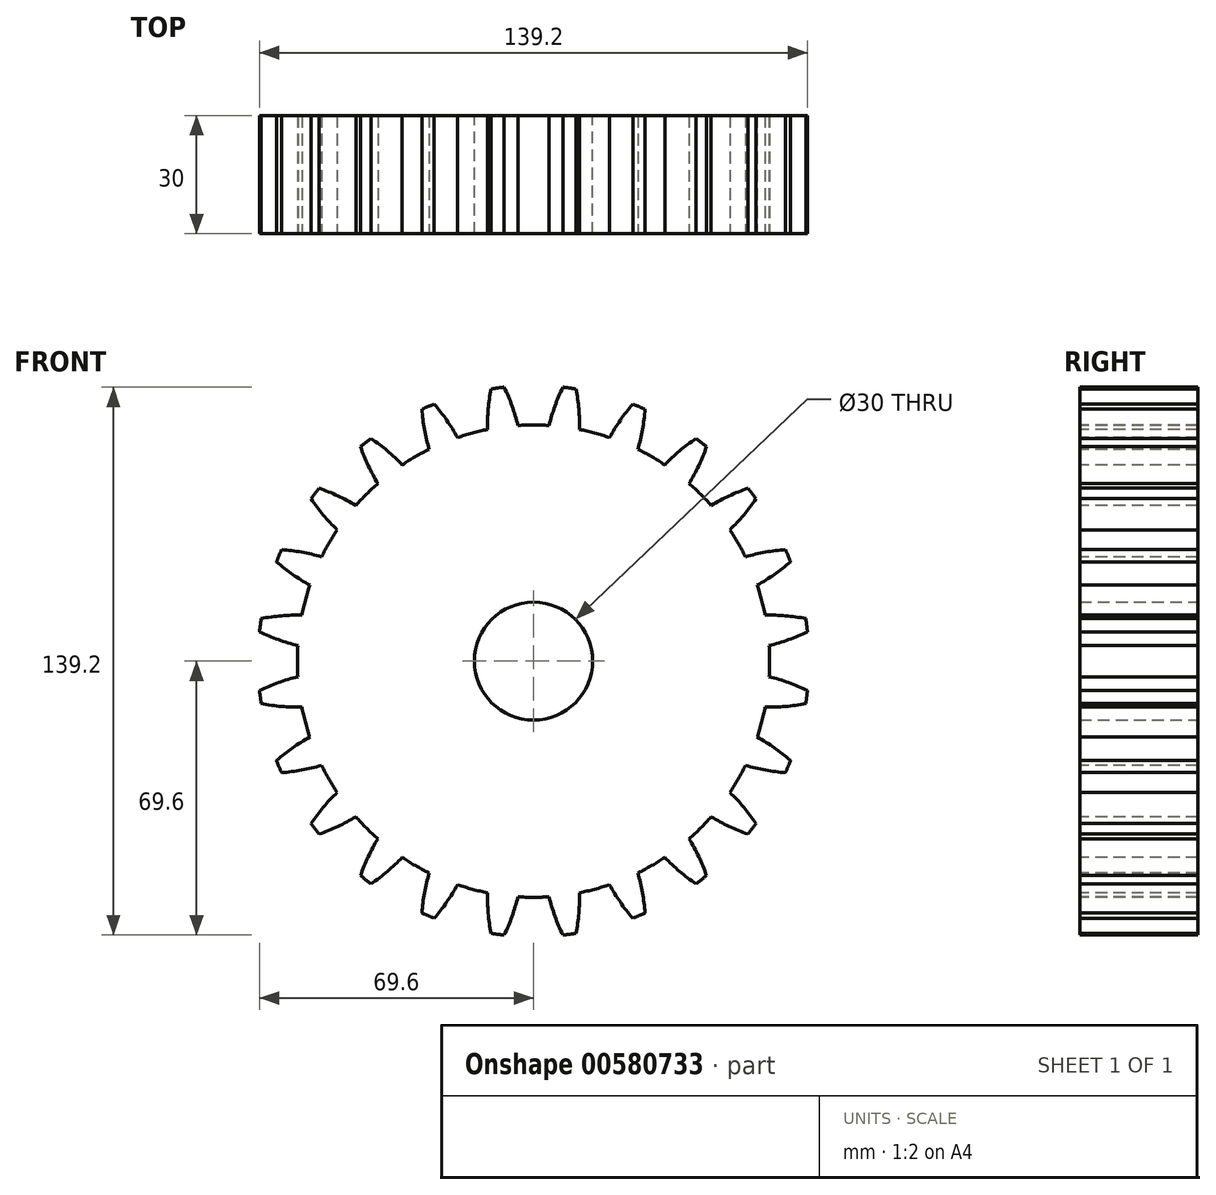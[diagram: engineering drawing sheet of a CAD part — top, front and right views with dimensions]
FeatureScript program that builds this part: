
annotation { "Feature Type Name" : "Feature", "Feature Type Description" : "" }
export const myFeature = defineFeature(function(context is Context, id is Id, definition is map)
    precondition{}
    {
        {
            var Q0;
            Q0=qCreatedBy(makeId("Front.planeOp"),FACE);
            var sketch = newSketch(context, id + "F0", { "sketchPlane" : qUnion([Q0])});
            skCircle(sketch, "E0", {"center": v(0, 0) * mm, "radius": 15 * mm});
            skCircle(sketch, "E1", {"center": v(0, 0) * mm, "radius": 70 * mm});
            skSolve(sketch);
        }
        {
            var Q0;
            Q0 = qSketchRegion(id + "F0", true);
            extrude(context, id + "F1", {"entities" : qUnion([Q0]), "depth" : 30 * mm, "offsetDistance" : 25 * mm});
        }
        {
            var Q0;
            Q0=makeQuery(id+"F1.opExtrude","CAP_FACE",FACE,{"disambiguationData":[OSD([sQuery(id+"F0.wireOp",EDGE,"E0"),sQuery(id+"F0.wireOp",EDGE,"E1")])],"isStart":false});
            var sketch = newSketch(context, id + "F2", { "sketchPlane" : qUnion([Q0])});
            skArc(sketch, "E2", {"start": v(8.7, 71.98) * mm, "mid": v(0, 72.5) * mm, "end": v(-8.7, 71.98) * mm});
            skArc(sketch, "E3", {"start": v(3.96, 59.87) * mm, "mid": v(0, 60) * mm, "end": v(-3.96, 59.87) * mm});
            skPoint(sketch, "E4", {"position": v(0, 48.69) * mm});
            skArc(sketch, "E5", {"start": v(8.7, 71.98) * mm, "mid": v(5.92, 66.08) * mm, "end": v(3.96, 59.87) * mm});
            skArc(sketch, "E6.MirrorC", {"start": v(-8.7, 71.98) * mm, "mid": v(-5.92, 66.08) * mm, "end": v(-3.96, 59.87) * mm});
            skArc(sketch, "E7.1.0", {"start": v(-10.22, 71.78) * mm, "mid": v(-18.76, 70.03) * mm, "end": v(-27.04, 67.27) * mm});
            skArc(sketch, "E7.1.1", {"start": v(-10.22, 71.78) * mm, "mid": v(-11.39, 65.36) * mm, "end": v(-11.67, 58.85) * mm});
            skArc(sketch, "E7.1.2", {"start": v(-11.67, 58.85) * mm, "mid": v(-15.53, 57.96) * mm, "end": v(-19.32, 56.8) * mm});
            skArc(sketch, "E7.1.3", {"start": v(-27.04, 67.27) * mm, "mid": v(-22.82, 62.3) * mm, "end": v(-19.32, 56.8) * mm});
            skArc(sketch, "E7.2.0", {"start": v(-28.45, 66.69) * mm, "mid": v(-36.25, 62.79) * mm, "end": v(-43.53, 57.98) * mm});
            skArc(sketch, "E7.2.1", {"start": v(-28.45, 66.69) * mm, "mid": v(-27.92, 60.2) * mm, "end": v(-26.5, 53.83) * mm});
            skArc(sketch, "E7.2.2", {"start": v(-26.5, 53.83) * mm, "mid": v(-30, 51.96) * mm, "end": v(-33.36, 49.87) * mm});
            skArc(sketch, "E7.2.3", {"start": v(-43.53, 57.98) * mm, "mid": v(-38.17, 54.27) * mm, "end": v(-33.36, 49.87) * mm});
            skArc(sketch, "E7.3.0", {"start": v(-44.74, 57.05) * mm, "mid": v(-51.27, 51.27) * mm, "end": v(-57.05, 44.74) * mm});
            skArc(sketch, "E7.3.1", {"start": v(-44.74, 57.05) * mm, "mid": v(-42.54, 50.91) * mm, "end": v(-39.53, 45.13) * mm});
            skArc(sketch, "E7.3.2", {"start": v(-39.53, 45.13) * mm, "mid": v(-42.43, 42.43) * mm, "end": v(-45.13, 39.53) * mm});
            skArc(sketch, "E7.3.3", {"start": v(-57.05, 44.74) * mm, "mid": v(-50.91, 42.54) * mm, "end": v(-45.13, 39.53) * mm});
            skArc(sketch, "E7.4.0", {"start": v(-57.98, 43.53) * mm, "mid": v(-62.79, 36.25) * mm, "end": v(-66.69, 28.45) * mm});
            skArc(sketch, "E7.4.1", {"start": v(-57.98, 43.53) * mm, "mid": v(-54.27, 38.17) * mm, "end": v(-49.87, 33.36) * mm});
            skArc(sketch, "E7.4.2", {"start": v(-49.87, 33.36) * mm, "mid": v(-51.96, 30) * mm, "end": v(-53.83, 26.5) * mm});
            skArc(sketch, "E7.4.3", {"start": v(-66.69, 28.45) * mm, "mid": v(-60.2, 27.92) * mm, "end": v(-53.83, 26.5) * mm});
            skArc(sketch, "E7.5.0", {"start": v(-67.27, 27.04) * mm, "mid": v(-70.03, 18.76) * mm, "end": v(-71.78, 10.22) * mm});
            skArc(sketch, "E7.5.1", {"start": v(-67.27, 27.04) * mm, "mid": v(-62.3, 22.82) * mm, "end": v(-56.8, 19.32) * mm});
            skArc(sketch, "E7.5.2", {"start": v(-56.8, 19.32) * mm, "mid": v(-57.96, 15.53) * mm, "end": v(-58.85, 11.67) * mm});
            skArc(sketch, "E7.5.3", {"start": v(-71.78, 10.22) * mm, "mid": v(-65.36, 11.39) * mm, "end": v(-58.85, 11.67) * mm});
            skArc(sketch, "E7.6.0", {"start": v(-71.98, 8.7) * mm, "mid": v(-72.5, 0) * mm, "end": v(-71.98, -8.7) * mm});
            skArc(sketch, "E7.6.1", {"start": v(-71.98, 8.7) * mm, "mid": v(-66.08, 5.92) * mm, "end": v(-59.87, 3.96) * mm});
            skArc(sketch, "E7.6.2", {"start": v(-59.87, 3.96) * mm, "mid": v(-60, 0) * mm, "end": v(-59.87, -3.96) * mm});
            skArc(sketch, "E7.6.3", {"start": v(-71.98, -8.7) * mm, "mid": v(-66.08, -5.92) * mm, "end": v(-59.87, -3.96) * mm});
            skArc(sketch, "E7.7.0", {"start": v(-71.78, -10.22) * mm, "mid": v(-70.03, -18.76) * mm, "end": v(-67.27, -27.04) * mm});
            skArc(sketch, "E7.7.1", {"start": v(-71.78, -10.22) * mm, "mid": v(-65.36, -11.39) * mm, "end": v(-58.85, -11.67) * mm});
            skArc(sketch, "E7.7.2", {"start": v(-58.85, -11.67) * mm, "mid": v(-57.96, -15.53) * mm, "end": v(-56.8, -19.32) * mm});
            skArc(sketch, "E7.7.3", {"start": v(-67.27, -27.04) * mm, "mid": v(-62.3, -22.82) * mm, "end": v(-56.8, -19.32) * mm});
            skArc(sketch, "E7.8.0", {"start": v(-66.69, -28.45) * mm, "mid": v(-62.79, -36.25) * mm, "end": v(-57.98, -43.53) * mm});
            skArc(sketch, "E7.8.1", {"start": v(-66.69, -28.45) * mm, "mid": v(-60.2, -27.92) * mm, "end": v(-53.83, -26.5) * mm});
            skArc(sketch, "E7.8.2", {"start": v(-53.83, -26.5) * mm, "mid": v(-51.96, -30) * mm, "end": v(-49.87, -33.36) * mm});
            skArc(sketch, "E7.8.3", {"start": v(-57.98, -43.53) * mm, "mid": v(-54.27, -38.17) * mm, "end": v(-49.87, -33.36) * mm});
            skArc(sketch, "E7.9.0", {"start": v(-57.05, -44.74) * mm, "mid": v(-51.27, -51.27) * mm, "end": v(-44.74, -57.05) * mm});
            skArc(sketch, "E7.9.1", {"start": v(-57.05, -44.74) * mm, "mid": v(-50.91, -42.54) * mm, "end": v(-45.13, -39.53) * mm});
            skArc(sketch, "E7.9.2", {"start": v(-45.13, -39.53) * mm, "mid": v(-42.43, -42.43) * mm, "end": v(-39.53, -45.13) * mm});
            skArc(sketch, "E7.9.3", {"start": v(-44.74, -57.05) * mm, "mid": v(-42.54, -50.91) * mm, "end": v(-39.53, -45.13) * mm});
            skArc(sketch, "E7.10.0", {"start": v(-43.53, -57.98) * mm, "mid": v(-36.25, -62.79) * mm, "end": v(-28.45, -66.69) * mm});
            skArc(sketch, "E7.10.1", {"start": v(-43.53, -57.98) * mm, "mid": v(-38.17, -54.27) * mm, "end": v(-33.36, -49.87) * mm});
            skArc(sketch, "E7.10.2", {"start": v(-33.36, -49.87) * mm, "mid": v(-30, -51.96) * mm, "end": v(-26.5, -53.83) * mm});
            skArc(sketch, "E7.10.3", {"start": v(-28.45, -66.69) * mm, "mid": v(-27.92, -60.2) * mm, "end": v(-26.5, -53.83) * mm});
            skArc(sketch, "E7.11.0", {"start": v(-27.04, -67.27) * mm, "mid": v(-18.76, -70.03) * mm, "end": v(-10.22, -71.78) * mm});
            skArc(sketch, "E7.11.1", {"start": v(-27.04, -67.27) * mm, "mid": v(-22.82, -62.3) * mm, "end": v(-19.32, -56.8) * mm});
            skArc(sketch, "E7.11.2", {"start": v(-19.32, -56.8) * mm, "mid": v(-15.53, -57.96) * mm, "end": v(-11.67, -58.85) * mm});
            skArc(sketch, "E7.11.3", {"start": v(-10.22, -71.78) * mm, "mid": v(-11.39, -65.36) * mm, "end": v(-11.67, -58.85) * mm});
            skArc(sketch, "E7.12.0", {"start": v(-8.7, -71.98) * mm, "mid": v(0, -72.5) * mm, "end": v(8.7, -71.98) * mm});
            skArc(sketch, "E7.12.1", {"start": v(-8.7, -71.98) * mm, "mid": v(-5.92, -66.08) * mm, "end": v(-3.96, -59.87) * mm});
            skArc(sketch, "E7.12.2", {"start": v(-3.96, -59.87) * mm, "mid": v(0, -60) * mm, "end": v(3.96, -59.87) * mm});
            skArc(sketch, "E7.12.3", {"start": v(8.7, -71.98) * mm, "mid": v(5.92, -66.08) * mm, "end": v(3.96, -59.87) * mm});
            skArc(sketch, "E7.13.0", {"start": v(10.22, -71.78) * mm, "mid": v(18.76, -70.03) * mm, "end": v(27.04, -67.27) * mm});
            skArc(sketch, "E7.13.1", {"start": v(10.22, -71.78) * mm, "mid": v(11.39, -65.36) * mm, "end": v(11.67, -58.85) * mm});
            skArc(sketch, "E7.13.2", {"start": v(11.67, -58.85) * mm, "mid": v(15.53, -57.96) * mm, "end": v(19.32, -56.8) * mm});
            skArc(sketch, "E7.13.3", {"start": v(27.04, -67.27) * mm, "mid": v(22.82, -62.3) * mm, "end": v(19.32, -56.8) * mm});
            skArc(sketch, "E7.14.0", {"start": v(28.45, -66.69) * mm, "mid": v(36.25, -62.79) * mm, "end": v(43.53, -57.98) * mm});
            skArc(sketch, "E7.14.1", {"start": v(28.45, -66.69) * mm, "mid": v(27.92, -60.2) * mm, "end": v(26.5, -53.83) * mm});
            skArc(sketch, "E7.14.2", {"start": v(26.5, -53.83) * mm, "mid": v(30, -51.96) * mm, "end": v(33.36, -49.87) * mm});
            skArc(sketch, "E7.14.3", {"start": v(43.53, -57.98) * mm, "mid": v(38.17, -54.27) * mm, "end": v(33.36, -49.87) * mm});
            skArc(sketch, "E7.15.0", {"start": v(44.74, -57.05) * mm, "mid": v(51.27, -51.27) * mm, "end": v(57.05, -44.74) * mm});
            skArc(sketch, "E7.15.1", {"start": v(44.74, -57.05) * mm, "mid": v(42.54, -50.91) * mm, "end": v(39.53, -45.13) * mm});
            skArc(sketch, "E7.15.2", {"start": v(39.53, -45.13) * mm, "mid": v(42.43, -42.43) * mm, "end": v(45.13, -39.53) * mm});
            skArc(sketch, "E7.15.3", {"start": v(57.05, -44.74) * mm, "mid": v(50.91, -42.54) * mm, "end": v(45.13, -39.53) * mm});
            skArc(sketch, "E7.16.0", {"start": v(57.98, -43.53) * mm, "mid": v(62.79, -36.25) * mm, "end": v(66.69, -28.45) * mm});
            skArc(sketch, "E7.16.1", {"start": v(57.98, -43.53) * mm, "mid": v(54.27, -38.17) * mm, "end": v(49.87, -33.36) * mm});
            skArc(sketch, "E7.16.2", {"start": v(49.87, -33.36) * mm, "mid": v(51.96, -30) * mm, "end": v(53.83, -26.5) * mm});
            skArc(sketch, "E7.16.3", {"start": v(66.69, -28.45) * mm, "mid": v(60.2, -27.92) * mm, "end": v(53.83, -26.5) * mm});
            skArc(sketch, "E7.17.0", {"start": v(67.27, -27.04) * mm, "mid": v(70.03, -18.76) * mm, "end": v(71.78, -10.22) * mm});
            skArc(sketch, "E7.17.1", {"start": v(67.27, -27.04) * mm, "mid": v(62.3, -22.82) * mm, "end": v(56.8, -19.32) * mm});
            skArc(sketch, "E7.17.2", {"start": v(56.8, -19.32) * mm, "mid": v(57.96, -15.53) * mm, "end": v(58.85, -11.67) * mm});
            skArc(sketch, "E7.17.3", {"start": v(71.78, -10.22) * mm, "mid": v(65.36, -11.39) * mm, "end": v(58.85, -11.67) * mm});
            skArc(sketch, "E7.18.0", {"start": v(71.98, -8.7) * mm, "mid": v(72.5, 0) * mm, "end": v(71.98, 8.7) * mm});
            skArc(sketch, "E7.18.1", {"start": v(71.98, -8.7) * mm, "mid": v(66.08, -5.92) * mm, "end": v(59.87, -3.96) * mm});
            skArc(sketch, "E7.18.2", {"start": v(59.87, -3.96) * mm, "mid": v(60, 0) * mm, "end": v(59.87, 3.96) * mm});
            skArc(sketch, "E7.18.3", {"start": v(71.98, 8.7) * mm, "mid": v(66.08, 5.92) * mm, "end": v(59.87, 3.96) * mm});
            skArc(sketch, "E7.19.0", {"start": v(71.78, 10.22) * mm, "mid": v(70.03, 18.76) * mm, "end": v(67.27, 27.04) * mm});
            skArc(sketch, "E7.19.1", {"start": v(71.78, 10.22) * mm, "mid": v(65.36, 11.39) * mm, "end": v(58.85, 11.67) * mm});
            skArc(sketch, "E7.19.2", {"start": v(58.85, 11.67) * mm, "mid": v(57.96, 15.53) * mm, "end": v(56.8, 19.32) * mm});
            skArc(sketch, "E7.19.3", {"start": v(67.27, 27.04) * mm, "mid": v(62.3, 22.82) * mm, "end": v(56.8, 19.32) * mm});
            skArc(sketch, "E7.20.0", {"start": v(66.69, 28.45) * mm, "mid": v(62.79, 36.25) * mm, "end": v(57.98, 43.53) * mm});
            skArc(sketch, "E7.20.1", {"start": v(66.69, 28.45) * mm, "mid": v(60.2, 27.92) * mm, "end": v(53.83, 26.5) * mm});
            skArc(sketch, "E7.20.2", {"start": v(53.83, 26.5) * mm, "mid": v(51.96, 30) * mm, "end": v(49.87, 33.36) * mm});
            skArc(sketch, "E7.20.3", {"start": v(57.98, 43.53) * mm, "mid": v(54.27, 38.17) * mm, "end": v(49.87, 33.36) * mm});
            skArc(sketch, "E7.21.0", {"start": v(57.05, 44.74) * mm, "mid": v(51.27, 51.27) * mm, "end": v(44.74, 57.05) * mm});
            skArc(sketch, "E7.21.1", {"start": v(57.05, 44.74) * mm, "mid": v(50.91, 42.54) * mm, "end": v(45.13, 39.53) * mm});
            skArc(sketch, "E7.21.2", {"start": v(45.13, 39.53) * mm, "mid": v(42.43, 42.43) * mm, "end": v(39.53, 45.13) * mm});
            skArc(sketch, "E7.21.3", {"start": v(44.74, 57.05) * mm, "mid": v(42.54, 50.91) * mm, "end": v(39.53, 45.13) * mm});
            skArc(sketch, "E8.3.22.0", {"start": v(43.53, 57.98) * mm, "mid": v(36.25, 62.79) * mm, "end": v(28.45, 66.69) * mm});
            skArc(sketch, "E8.4.22.0", {"start": v(43.53, 57.98) * mm, "mid": v(38.17, 54.27) * mm, "end": v(33.36, 49.87) * mm});
            skArc(sketch, "E8.8.22.0", {"start": v(33.36, 49.87) * mm, "mid": v(30, 51.96) * mm, "end": v(26.5, 53.83) * mm});
            skArc(sketch, "E8.12.22.0", {"start": v(28.45, 66.69) * mm, "mid": v(27.92, 60.2) * mm, "end": v(26.5, 53.83) * mm});
            skArc(sketch, "E8.3.23.0", {"start": v(27.04, 67.27) * mm, "mid": v(18.76, 70.03) * mm, "end": v(10.22, 71.78) * mm});
            skArc(sketch, "E8.4.23.0", {"start": v(27.04, 67.27) * mm, "mid": v(22.82, 62.3) * mm, "end": v(19.32, 56.8) * mm});
            skArc(sketch, "E8.8.23.0", {"start": v(19.32, 56.8) * mm, "mid": v(15.53, 57.96) * mm, "end": v(11.67, 58.85) * mm});
            skArc(sketch, "E8.12.23.0", {"start": v(10.22, 71.78) * mm, "mid": v(11.39, 65.36) * mm, "end": v(11.67, 58.85) * mm});
            skSolve(sketch);
        }
        {
            var Q0;
            Q0 = qSketchRegion(id + "F2", true);
            extrude(context, id + "F3", {"entities" : qUnion([Q0]), "operationType" : NewBodyOperationType.REMOVE, "oppositeDirection" : true, "depth" : 31 * mm, "offsetDistance" : 25 * mm});
        }
    });
